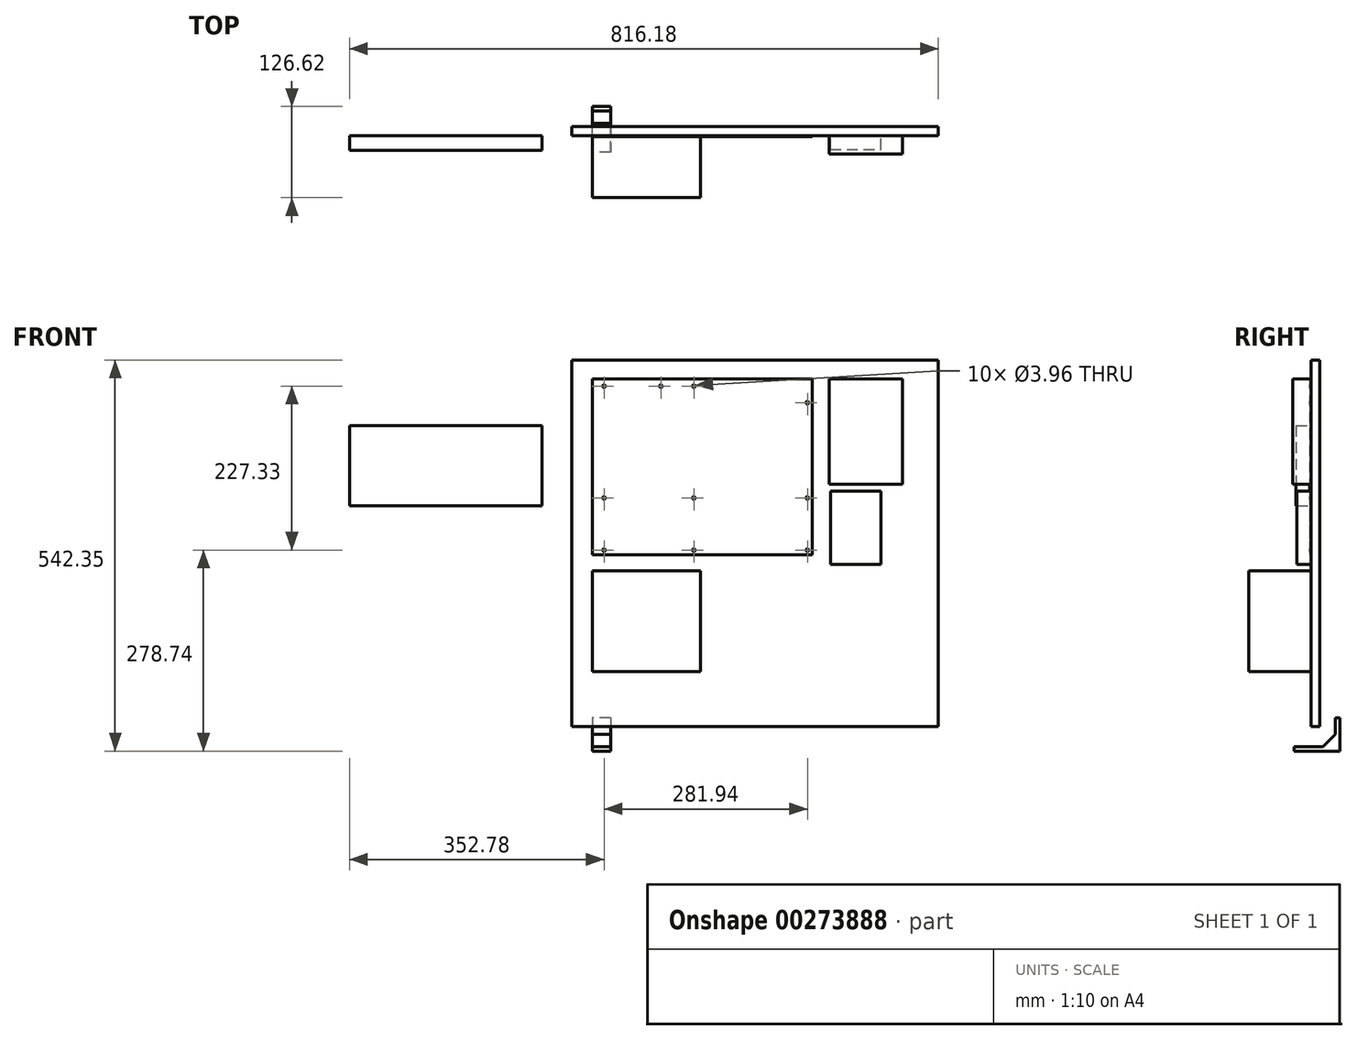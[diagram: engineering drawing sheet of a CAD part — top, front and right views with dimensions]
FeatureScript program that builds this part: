
annotation { "Feature Type Name" : "Feature", "Feature Type Description" : "" }
export const myFeature = defineFeature(function(context is Context, id is Id, definition is map)
    precondition{}
    {
        {
            var Q0;
            Q0=qCreatedBy(makeId("Front.planeOp"),FACE);
            var sketch = newSketch(context, id + "F0", { "sketchPlane" : qUnion([Q0])});
            skCircle(sketch, "E0", {"center": v(16.51, -10.16) * mm, "radius": 1.98 * mm});
            skCircle(sketch, "E1", {"center": v(140.97, -10.16) * mm, "radius": 1.98 * mm});
            skCircle(sketch, "E2", {"center": v(95.25, -10.16) * mm, "radius": 1.98 * mm});
            skCircle(sketch, "E3", {"center": v(298.45, -33.02) * mm, "radius": 1.98 * mm});
            skCircle(sketch, "E4", {"center": v(298.45, -165.1) * mm, "radius": 1.98 * mm});
            skCircle(sketch, "E5", {"center": v(298.45, -237.49) * mm, "radius": 1.98 * mm});
            skCircle(sketch, "E6", {"center": v(140.97, -165.1) * mm, "radius": 1.98 * mm});
            skCircle(sketch, "E7", {"center": v(140.97, -237.5) * mm, "radius": 1.98 * mm});
            skCircle(sketch, "E8", {"center": v(16.51, -165.1) * mm, "radius": 1.98 * mm});
            skCircle(sketch, "E9", {"center": v(16.51, -237.5) * mm, "radius": 1.98 * mm});
            skLineSegment(sketch, "E10.bottom", {"start": v(0, 0) * mm, "end": v(304.8, 0) * mm});
            skLineSegment(sketch, "E10.top", {"start": v(0, -243.84) * mm, "end": v(304.8, -243.84) * mm});
            skLineSegment(sketch, "E10.left", {"start": v(0, 0) * mm, "end": v(0, -243.84) * mm});
            skLineSegment(sketch, "E10.right", {"start": v(304.8, 0) * mm, "end": v(304.8, -243.84) * mm});
            skSolve(sketch);
        }
        {
            var Q0;
            Q0=qSketchRegion(id+"F0",true);
            extrude(context, id + "F1", {"entities" : qUnion([Q0]), "depth" : 1.57 * mm});
        }
        {
            var Q0;
            Q0=qCreatedBy(makeId("Front.planeOp"),FACE);
            var sketch = newSketch(context, id + "F2", { "sketchPlane" : qUnion([Q0])});
            skLineSegment(sketch, "E11.bottom", {"start": v(150, -406.22) * mm, "end": v(0, -406.22) * mm});
            skLineSegment(sketch, "E11.top", {"start": v(150, -266.22) * mm, "end": v(0, -266.22) * mm});
            skLineSegment(sketch, "E11.left", {"start": v(150, -406.22) * mm, "end": v(150, -266.22) * mm});
            skLineSegment(sketch, "E11.right", {"start": v(0, -406.22) * mm, "end": v(0, -266.22) * mm});
            skSolve(sketch);
        }
        {
            var Q0;
            Q0=qSketchRegion(id+"F2",true);
            extrude(context, id + "F3", {"entities" : qUnion([Q0]), "depth" : 86 * mm});
        }
        {
            var Q0;
            Q0=qCreatedBy(makeId("Front.planeOp"),FACE);
            var sketch = newSketch(context, id + "F4", { "sketchPlane" : qUnion([Q0])});
            skLineSegment(sketch, "E12.bottom", {"start": v(-69.57, -65.05) * mm, "end": v(-336.27, -65.05) * mm});
            skLineSegment(sketch, "E12.top", {"start": v(-69.57, -176.2) * mm, "end": v(-336.27, -176.2) * mm});
            skLineSegment(sketch, "E12.left", {"start": v(-69.57, -65.05) * mm, "end": v(-69.57, -176.2) * mm});
            skLineSegment(sketch, "E12.right", {"start": v(-336.27, -65.05) * mm, "end": v(-336.27, -176.2) * mm});
            skSolve(sketch);
        }
        {
            var Q0;
            Q0=qSketchRegion(id+"F4",true);
            extrude(context, id + "F5", {"entities" : qUnion([Q0]), "operationType" : NewBodyOperationType.ADD, "depth" : 20.32 * mm});
        }
        {
            var Q0;
            Q0=qCreatedBy(makeId("Front.planeOp"),FACE);
            var sketch = newSketch(context, id + "F6", { "sketchPlane" : qUnion([Q0])});
            skLineSegment(sketch, "E13.bottom", {"start": v(328.46, -146.05) * mm, "end": v(430.06, -146.05) * mm});
            skLineSegment(sketch, "E13.top", {"start": v(328.46, 0) * mm, "end": v(430.06, 0) * mm});
            skLineSegment(sketch, "E13.left", {"start": v(328.46, -146.05) * mm, "end": v(328.46, 0) * mm});
            skLineSegment(sketch, "E13.right", {"start": v(430.06, -146.05) * mm, "end": v(430.06, 0) * mm});
            skSolve(sketch);
        }
        {
            var Q0;
            Q0=qSketchRegion(id+"F6",true);
            extrude(context, id + "F7", {"entities" : qUnion([Q0]), "depth" : 25.4 * mm});
        }
        {
            var Q0;
            Q0=qCreatedBy(makeId("Front.planeOp"),FACE);
            var sketch = newSketch(context, id + "F8", { "sketchPlane" : qUnion([Q0])});
            skLineSegment(sketch, "E14.bottom", {"start": v(330.23, -257.37) * mm, "end": v(400.08, -257.37) * mm});
            skLineSegment(sketch, "E14.top", {"start": v(330.23, -155.77) * mm, "end": v(400.08, -155.77) * mm});
            skLineSegment(sketch, "E14.left", {"start": v(330.23, -257.37) * mm, "end": v(330.23, -155.77) * mm});
            skLineSegment(sketch, "E14.right", {"start": v(400.08, -257.37) * mm, "end": v(400.08, -155.77) * mm});
            skSolve(sketch);
        }
        {
            var Q0;
            Q0=qSketchRegion(id+"F8",true);
            extrude(context, id + "F9", {"entities" : qUnion([Q0]), "depth" : 19.05 * mm});
        }
        {
            var Q0;
            Q0=qCreatedBy(makeId("Front.planeOp"),FACE);
            var sketch = newSketch(context, id + "F10", { "sketchPlane" : qUnion([Q0])});
            skLineSegment(sketch, "E15.bottom", {"start": v(-28.09, 26.12) * mm, "end": v(479.91, 26.12) * mm});
            skLineSegment(sketch, "E15.top", {"start": v(-28.09, -481.88) * mm, "end": v(479.91, -481.88) * mm});
            skLineSegment(sketch, "E15.left", {"start": v(-28.09, 26.12) * mm, "end": v(-28.09, -481.88) * mm});
            skLineSegment(sketch, "E15.right", {"start": v(479.91, 26.12) * mm, "end": v(479.91, -481.88) * mm});
            skSolve(sketch);
        }
        {
            var Q0;
            Q0=makeQuery(id+"F10.imprint","IMPRINT",FACE,{"disambiguationData":[TD([[makeQuery(id+"F10.imprint","IMPRINT",EDGE,{"derivedFrom":sQuery(id+"F10.wireOp",EDGE,"E15.bottom")}),-1.0]])]});
            extrude(context, id + "F11", {"entities" : qUnion([Q0]), "oppositeDirection" : true, "depth" : 12.7 * mm});
        }
        {
            var Q0;
            Q0=qCreatedBy(makeId("Right.planeOp"),FACE);
            var sketch = newSketch(context, id + "F12", { "sketchPlane" : qUnion([Q0])});
            skLineSegment(sketch, "E16.bottom", {"start": v(34.27, -470.07) * mm, "end": v(40.62, -470.07) * mm});
            skLineSegment(sketch, "E16.left", {"start": v(34.27, -470.07) * mm, "end": v(34.27, -492.65) * mm});
            skLineSegment(sketch, "E16.right", {"start": v(40.62, -470.07) * mm, "end": v(40.62, -516.23) * mm});
            skLineSegment(sketch, "E17.top", {"start": v(17.04, -509.88) * mm, "end": v(-22.88, -509.88) * mm});
            skLineSegment(sketch, "E17.right", {"start": v(-22.88, -516.23) * mm, "end": v(-22.88, -509.88) * mm});
            skLineSegment(sketch, "E18", {"start": v(-22.88, -516.23) * mm, "end": v(40.62, -516.23) * mm});
            skLineSegment(sketch, "E19", {"start": v(17.04, -509.88) * mm, "end": v(34.27, -492.65) * mm});
            skSolve(sketch);
        }
        {
            var Q0;
            Q0=qSketchRegion(id+"F12",true);
            extrude(context, id + "F13", {"entities" : qUnion([Q0]), "depth" : 25.4 * mm});
        }
    });
